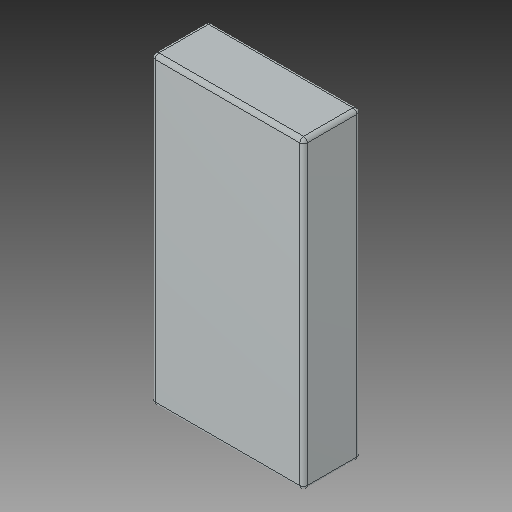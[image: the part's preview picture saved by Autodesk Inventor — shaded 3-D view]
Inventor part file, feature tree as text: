
AUTODESK INVENTOR PART (.ipt)
format: ipt  version: 2019.4 (Build 234330000, 330)  size: 100,864 bytes
history: mixed  units: mm
features: fillet x1, imported_body x1
ambient origin geometry x8: Origin, YZ Plane, XZ Plane, XY Plane, X Axis, Y Axis, Z Axis, Center Point
bodies: Solid1 (imported_parasolid)
feature tree (2):
  fillet  "Fillet1"  [1 undecoded]
  imported_body  NMx_Import_Brep_tag  [imported B-rep: ~26 faces, bbox_mm=[4.0, 8.0, 1.5]]
note: 1 required parameter value undecoded (feature->parameter linkage not recoverable at this tier; creation-order binding heuristic only, values carry confidence <= 0.55)
